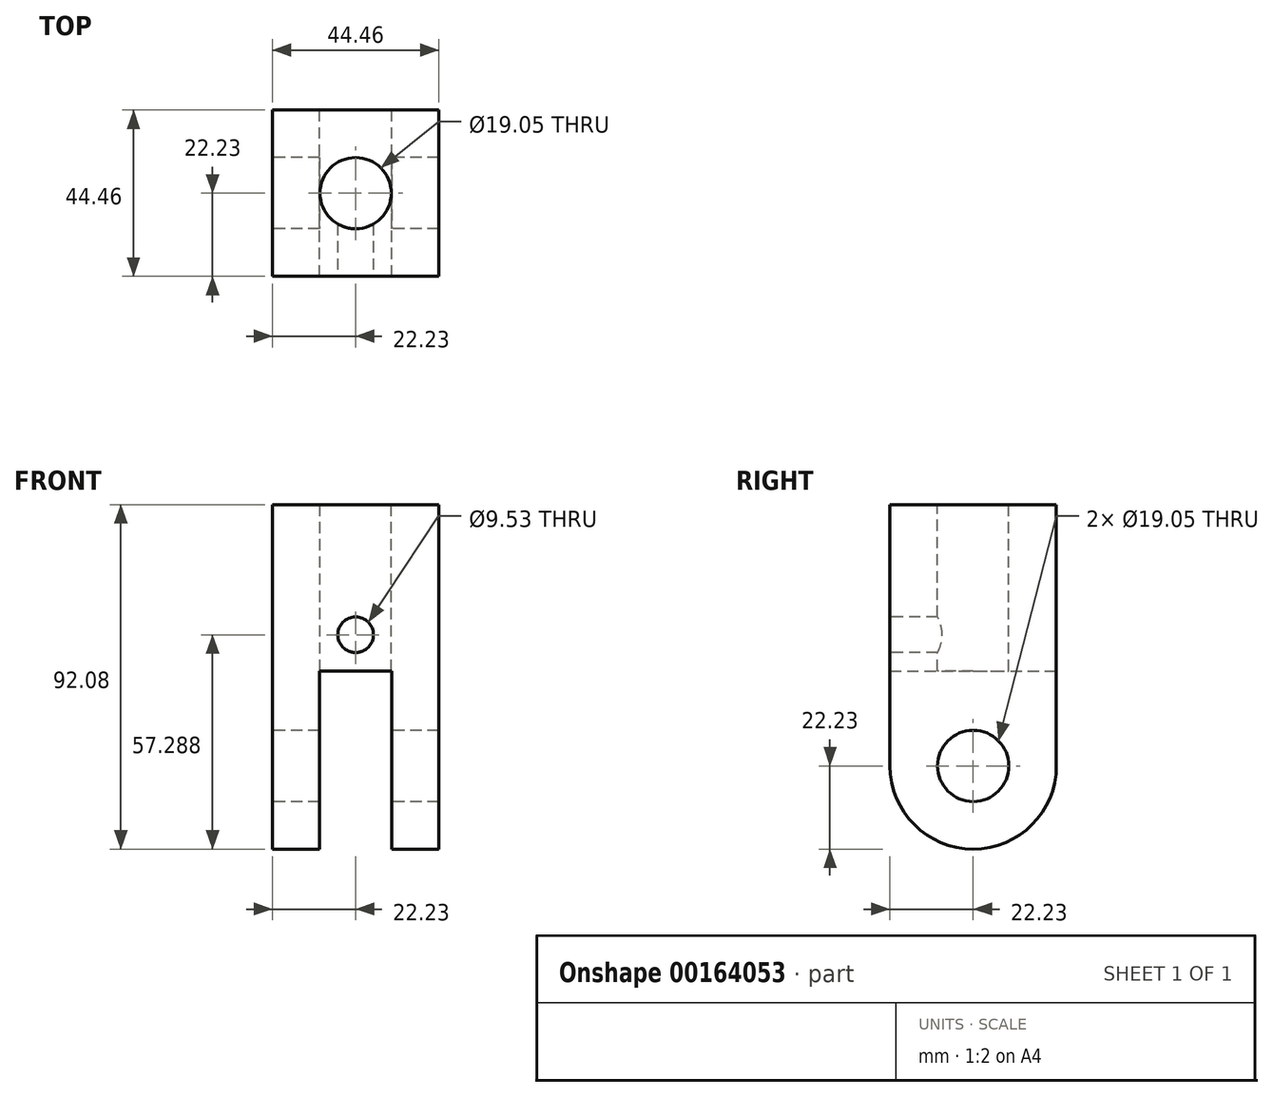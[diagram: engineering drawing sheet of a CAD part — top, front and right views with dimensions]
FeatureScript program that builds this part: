
annotation { "Feature Type Name" : "Feature", "Feature Type Description" : "" }
export const myFeature = defineFeature(function(context is Context, id is Id, definition is map)
    precondition{}
    {
        {
            var Q0;
            Q0=qCreatedBy(makeId("Right.planeOp"),FACE);
            var sketch = newSketch(context, id + "F0", { "sketchPlane" : qUnion([Q0])});
            skCircle(sketch, "E0", {"center": v(0, 0) * mm, "radius": 9.53 * mm});
            skArc(sketch, "E1", {"start": v(-22.23, 0) * mm, "mid": v(0, -22.23) * mm, "end": v(22.23, 0) * mm});
            skLineSegment(sketch, "E2", {"start": v(-22.23, 0) * mm, "end": v(-22.23, 69.85) * mm});
            skLineSegment(sketch, "E3", {"start": v(-22.23, 69.85) * mm, "end": v(0, 69.85) * mm});
            skLineSegment(sketch, "E4.0.MirrorCS", {"start": v(22.23, 0) * mm, "end": v(22.23, 69.85) * mm});
            skLineSegment(sketch, "E5.0.MirrorCS", {"start": v(22.23, 69.85) * mm, "end": v(0, 69.85) * mm});
            skSolve(sketch);
        }
        {
            var Q0;
            Q0=qSketchRegion(id+"F0",true);
            extrude(context, id + "F1", {"entities" : qUnion([Q0]), "endBound" : BoundingType.SYMMETRIC, "depth" : 44.45 * mm});
        }
        {
            var Q0;
            Q0=makeQuery(id+"F1.opExtrude","SWEPT_FACE",FACE,{"disambiguationData":[OSD([sQuery(id+"F0.wireOp",EDGE,"E4.0.MirrorCS")])]});
            var sketch = newSketch(context, id + "F2", { "sketchPlane" : qUnion([Q0])});
            skLineSegment(sketch, "E6", {"start": v(0, 69.85) * mm, "end": v(0, -28.46) * mm, "construction": true});
            skLineSegment(sketch, "E7.0", {"start": v(-22.23, 25.4) * mm, "end": v(22.23, 25.4) * mm, "construction": true});
            skLineSegment(sketch, "E8.0", {"start": v(-9.65, 69.85) * mm, "end": v(-9.65, -28.46) * mm, "construction": true});
            skLineSegment(sketch, "E9.0.MirrorCS", {"start": v(9.65, 69.85) * mm, "end": v(9.65, -28.46) * mm, "construction": true});
            skLineSegment(sketch, "E10.bottom", {"start": v(-9.65, 25.4) * mm, "end": v(9.65, 25.4) * mm});
            skLineSegment(sketch, "E10.top", {"start": v(-9.65, -28.46) * mm, "end": v(9.65, -28.46) * mm});
            skLineSegment(sketch, "E10.left", {"start": v(-9.65, 25.4) * mm, "end": v(-9.65, -28.46) * mm});
            skLineSegment(sketch, "E10.right", {"start": v(9.65, 25.4) * mm, "end": v(9.65, -28.46) * mm});
            skSolve(sketch);
        }
        {
            var Q0;
            {var subQ6=sQuery(id+"F2.wireOp",EDGE,"E10.top");var subQ7=sQuery(id+"F2.wireOp",EDGE,"E10.bottom");Q0=qUnion([makeQuery(id+"F2.imprint","IMPRINT",FACE,{"disambiguationData":[TD([[makeQuery(id+"F2.imprint","IMPRINT",EDGE,{"derivedFrom":subQ6}),1.0]])]}),makeQuery(id+"F2.imprint","IMPRINT",FACE,{"disambiguationData":[TD([[makeQuery(id+"F2.imprint","IMPRINT",EDGE,{"derivedFrom":subQ7}),-1.0]])]})]);}
            extrude(context, id + "F3", {"entities" : qUnion([Q0]), "operationType" : NewBodyOperationType.REMOVE, "endBound" : BoundingType.THROUGH_ALL, "oppositeDirection" : true, "depth" : 25.4 * mm});
        }
        {
            var Q0;
            Q0=makeQuery(id+"F1.opExtrude","SWEPT_FACE",FACE,{"disambiguationData":[OSD([sQuery(id+"F0.wireOp",EDGE,"E5.0.MirrorCS")])]});
            var sketch = newSketch(context, id + "F4", { "sketchPlane" : qUnion([Q0])});
            skCircle(sketch, "E11", {"center": v(0, 0) * mm, "radius": 9.52 * mm});
            skSolve(sketch);
        }
        {
            var Q0;
            Q0=makeQuery(id+"F4.imprint","IMPRINT",FACE,{"disambiguationData":[TD([[makeQuery(id+"F4.imprint","IMPRINT",EDGE,{"derivedFrom":sQuery(id+"F4.wireOp",EDGE,"E11")}),1.0]])]});
            extrude(context, id + "F5", {"entities" : qUnion([Q0]), "operationType" : NewBodyOperationType.REMOVE, "endBound" : BoundingType.THROUGH_ALL, "oppositeDirection" : true, "depth" : 25.4 * mm});
        }
        {
            var Q0;
            Q0=makeQuery(id+"F1.opExtrude","SWEPT_FACE",FACE,{"disambiguationData":[OSD([sQuery(id+"F0.wireOp",EDGE,"E2")])]});
            var sketch = newSketch(context, id + "F6", { "sketchPlane" : qUnion([Q0])});
            skLineSegment(sketch, "E12.0", {"start": v(22.23, 69.98) * mm, "end": v(-22.23, 69.98) * mm, "construction": true});
            skLineSegment(sketch, "E13.0", {"start": v(22.23, 35.06) * mm, "end": v(-22.23, 35.06) * mm, "construction": true});
            skCircle(sketch, "E14", {"center": v(0, 35.06) * mm, "radius": 4.76 * mm});
            skSolve(sketch);
        }
        {
            var Q0;
            Q0=makeQuery(id+"F6.imprint","IMPRINT",FACE,{"disambiguationData":[TD([[makeQuery(id+"F6.imprint","IMPRINT",EDGE,{"derivedFrom":sQuery(id+"F6.wireOp",EDGE,"E14")}),1.0]])]});
            var Q1;
            Q1=makeQuery(id+"F5.boolean.opBoolean","COPY",FACE,{"derivedFrom":makeQuery(id+"F5.opExtrude","SWEPT_FACE",FACE,{"disambiguationData":[OSD([sQuery(id+"F4.wireOp",EDGE,"E11")])]})});
            extrude(context, id + "F7", {"entities" : qUnion([Q0]), "operationType" : NewBodyOperationType.REMOVE, "endBound" : BoundingType.UP_TO_SURFACE, "oppositeDirection" : true, "endBoundEntityFace" : qUnion([Q1]), "depth" : 25.4 * mm});
        }
    });
